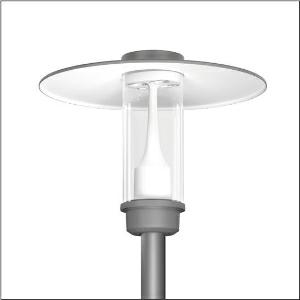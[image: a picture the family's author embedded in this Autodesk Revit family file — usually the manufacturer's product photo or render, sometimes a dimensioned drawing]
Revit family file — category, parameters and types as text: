
# Revit family: litepole_2_iq___p1_0a_5xa5425bf14h_a5ac
name_source: partatom
category: Lighting Fixtures
units: mm (PartAtom-declared; Revit-internal decimal feet)

## family parameters
Cut with Voids When Loaded = No
Host = Face
Light Source = No
Part Type = Normal
Room Calculation Point = No
Round Connector Dimension = Use Diameter
Shared = No

## types (1)
- --- (1 x LED, 1520 lm, 12.9 W, 2200K)
    Apparent Load = 13 VA
    CIE Flux Codes = 33 62 89 96 100
    Color Rendering = 70
    Color Temperature = 2200K
    Default Elevation = 1800 mm
    Description = Litepole 2 iQ, mast luminaire, Module 540 iQ-SR, primary light control with 3 zone facetted reflector, of plastic, silver coated, highly specular, structured, primary optical cover: cover, of PMMA, transparent, light distribution: P1.0a, light emission: direct distribution, primary light characteristic: strongly asymmetric, installation type: post-top, LED, High Power LED, rated luminous flux: 1.520lm, luminous efficacy: 118lm/W, light colour: 722, colour temperature: 2200K, control gear: ECG iQ, control: presetting dimming logarithmic, Street-Remote, Auto-Match, Temp-Guard, Lumen-Switch, Night-Set, Smart-Wire, Light-Fading, Desk-Remote (wireless, voltage-free reading and setting of iQ features in the workshop via application-optimized NFC function/RFID function), optimised constant luminous flux control (CLO 2.0), with terminal, 6-pole, max. 2.5mm², mains connection: 230..240V, AC, 50/60Hz, start of lifetime: 13W, end of service life: 13W, reduction: 6W, luminaire housing, upper part, of aluminium, coated, Siteco® metallic grey (DB 702S), diameter: 750mm, height: 590mm, spigot size: d x l = 76 x 70mm (post-top) | with reducer (optional accessory) 60 x 70mm, post-top mast mounting element, of diecast aluminium, coated, Siteco® metallic grey (DB 702S), Module 540 iQ-SR, traffic white (RAL 9016), equipment: standard, protection rating (complete): IP65, insulation class (complete): insulation class II (safety insulation), certification: CE, ENEC, VDE, packaging unit: 1 piece

Light Distribution: P1.0a
    Height = 590 mm
    Lamp = 1 x LED
    Lamp Light Flux = 1520 lm
    Lamp Power = 12.9 W
    Lamp count = 1
    Length = 750 mm
    Luminous efficacy = 118 lm/W
    Manufacturer = Siteco
    ModVariant = No
    Model = 5XA5425BF14H
    Number of Poles = 1
    OnlyDefault = Yes
    Power Factor = 1
    Product Name = Litepole 2 iQ | P1.0a
    Product group = mast luminaire | pylon top
    ProductGroupID = 6100
    Protection Class = Protection class II
    Protection Degree = IP 65
    RLX_Detail_Level = 1
    RLX_Emergency_Light_Flux = 0 lm
    RLX_Emergency_Type = 0
    RLX_Emergency_Type_DB = No
    RlxData = <blob elided: 138705 chars, md5=72ced39f>
    Socket = socket
    Standby Power = 0 W
    System Light Flux = 1520 lm
    System Power = 13 W
    Type Comments = factory setting: luminous flux: 100 % | dim-lin: 254 | 516 mA
    Type Image = l_1006518.jpg
    URL = http://relux.com
    VarID = @adj_126857
    Voltage = 0 V
    Weight = 0.00 kg
    Width = 0 mm  [stored 0 ft]

note: [stored X ft] marks values corroborated as IEEE doubles in the binary element streams (Revit-internal decimal feet)

## geometry (parser evidence)
native form markers: Blend x4, Sweep x9
no freeform markers — native parametric forms only
